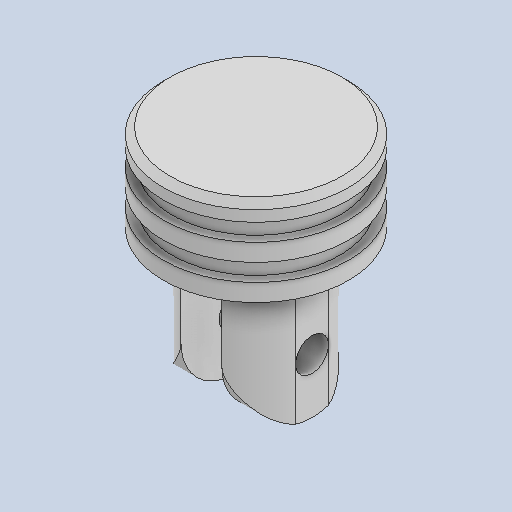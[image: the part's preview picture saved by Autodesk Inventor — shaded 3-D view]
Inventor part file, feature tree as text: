
AUTODESK INVENTOR PART (.ipt)
format: ipt  version: 2023 (Build 270158000, 158)  size: 339,968 bytes
history: native  units: in
note: dims shown in document units (in); Inventor stores cm internally (conversion verified against a paired STEP export)
features: sketch x3, extrude x2, revolve x1, chamfer x1, fillet x1
ambient origin geometry x8: Origin, YZ Plane, XZ Plane, XY Plane, X Axis, Y Axis, Z Axis, Center Point
bodies: Solid1 (feature_tree)
feature tree (8):
  revolve  "Revolution1"  [1 undecoded]
  extrude  "Extrusion2"  Depth=0.132in
  chamfer  "Chamfer1"  Distance=0.132in
  fillet  "Fillet1"  Radius=0.066in
  extrude  "Extrusion3"  Depth=0.125in
  sketch  "Sketch1"  dims[d0=0.7017in d1=0.132in]
  sketch  "Sketch2"  dims[d2=0.066in d3=0.132in]
  sketch  "Sketch3"  dims[d4=0.066in d5=0.132in d6=0.066in d7=0.132in d8=0.066in d9=0.132in d10=90.0deg d18=0.125in d19=1.25in d20=0.0in d21=0.05in d22=0.125in d23=45.0deg d24=0.125in d25=1.25in d26=0.0in]
note: 1 required parameter value undecoded (feature->parameter linkage not recoverable at this tier; creation-order binding heuristic only, values carry confidence <= 0.55)
